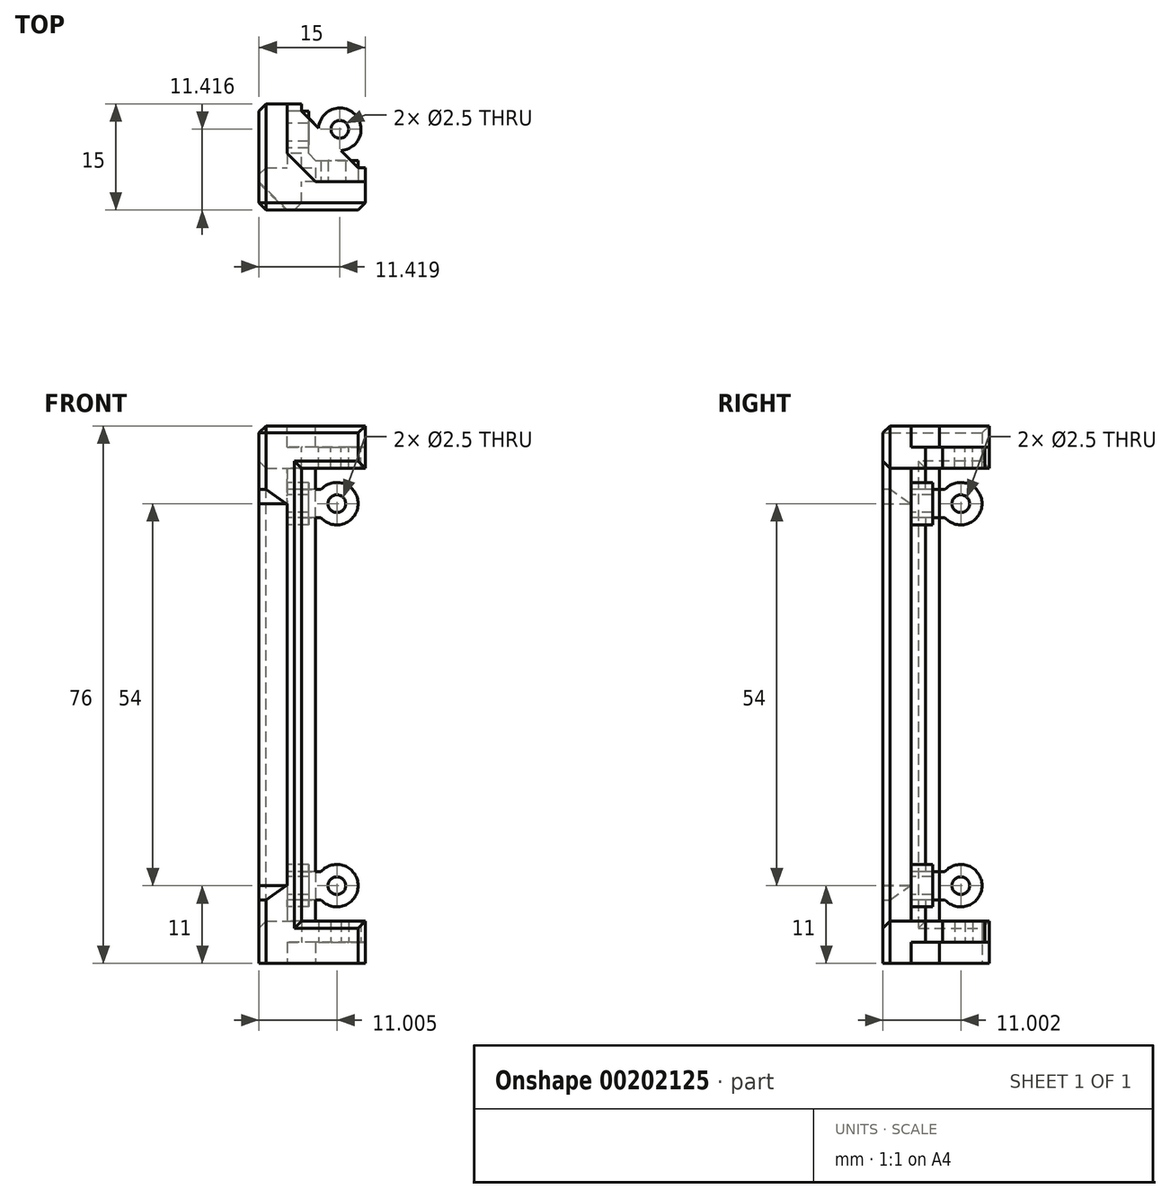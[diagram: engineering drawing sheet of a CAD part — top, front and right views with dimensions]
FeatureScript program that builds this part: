
annotation { "Feature Type Name" : "Feature", "Feature Type Description" : "" }
export const myFeature = defineFeature(function(context is Context, id is Id, definition is map)
    precondition{}
    {
        {
            var Q0;
            Q0=qCreatedBy(makeId("Top.planeOp"),FACE);
            var sketch = newSketch(context, id + "F0", { "sketchPlane" : qUnion([Q0])});
            skLineSegment(sketch, "E0", {"start": v(-30.7, 8.8) * mm, "end": v(-30.7, -6.2) * mm});
            skLineSegment(sketch, "E1", {"start": v(-30.7, -6.2) * mm, "end": v(-15.7, -6.2) * mm});
            skLineSegment(sketch, "E2", {"start": v(-30.7, 8.8) * mm, "end": v(-29.7, 8.8) * mm});
            skLineSegment(sketch, "E3", {"start": v(-15.7, -6.2) * mm, "end": v(-15.7, -5.2) * mm});
            skLineSegment(sketch, "E4", {"start": v(-29.7, 8.8) * mm, "end": v(-24.7, 8.8) * mm});
            skLineSegment(sketch, "E5", {"start": v(-15.7, -5.2) * mm, "end": v(-15.7, -0.2) * mm});
            skLineSegment(sketch, "E6", {"start": v(-24.7, 8.8) * mm, "end": v(-24.7, -0.2) * mm});
            skLineSegment(sketch, "E7", {"start": v(-24.7, -0.2) * mm, "end": v(-15.7, -0.2) * mm});
            skSolve(sketch);
        }
        {
            var Q0;
            Q0=makeQuery(id+"F0.imprint","IMPRINT",FACE,{"disambiguationData":[TD([[makeQuery(id+"F0.imprint","IMPRINT",EDGE,{"derivedFrom":sQuery(id+"F0.wireOp",EDGE,"E0")}),1.0]])]});
            extrude(context, id + "F1", {"entities" : qUnion([Q0]), "depth" : 6 * mm});
        }
        {
            var Q0;
            Q0=makeQuery(id+"F1.opExtrude","CAP_FACE",FACE,{"disambiguationData":[OSD([sQuery(id+"F0.wireOp",EDGE,"E0"),sQuery(id+"F0.wireOp",EDGE,"E1"),sQuery(id+"F0.wireOp",EDGE,"E2"),sQuery(id+"F0.wireOp",EDGE,"E3"),sQuery(id+"F0.wireOp",EDGE,"E4"),sQuery(id+"F0.wireOp",EDGE,"E5"),sQuery(id+"F0.wireOp",EDGE,"E6"),sQuery(id+"F0.wireOp",EDGE,"E7")])],"isStart":false});
            var sketch = newSketch(context, id + "F2", { "sketchPlane" : qUnion([Q0])});
            skLineSegment(sketch, "E8.top", {"start": v(-30.7, -0.2) * mm, "end": v(-24.7, -0.2) * mm});
            skLineSegment(sketch, "E9", {"start": v(-24.7, -0.2) * mm, "end": v(-24.7, 1.8) * mm});
            skLineSegment(sketch, "E10", {"start": v(-24.7, 1.8) * mm, "end": v(-26.7, 1.8) * mm});
            skLineSegment(sketch, "E11", {"start": v(-26.7, 1.8) * mm, "end": v(-26.7, -0.2) * mm});
            skLineSegment(sketch, "E12", {"start": v(-24.7, -0.2) * mm, "end": v(-22.7, -0.2) * mm});
            skLineSegment(sketch, "E13", {"start": v(-22.7, -0.2) * mm, "end": v(-22.7, -2.2) * mm});
            skLineSegment(sketch, "E14", {"start": v(-22.7, -2.2) * mm, "end": v(-24.7, -2.2) * mm});
            skLineSegment(sketch, "E15", {"start": v(-24.7, -6.2) * mm, "end": v(-29.7, -6.2) * mm});
            skLineSegment(sketch, "E16", {"start": v(-24.7, -6.2) * mm, "end": v(-24.7, -2.2) * mm});
            skLineSegment(sketch, "E17", {"start": v(-24.7, -0.2) * mm, "end": v(-24.7, -2.2) * mm});
            skLineSegment(sketch, "E18", {"start": v(-30.7, -0.2) * mm, "end": v(-30.7, -5.2) * mm});
            skLineSegment(sketch, "E19", {"start": v(-30.7, -5.2) * mm, "end": v(-29.7, -6.2) * mm});
            skSolve(sketch);
        }
        {
            var Q0;
            Q0=makeQuery(id+"F2.imprint","IMPRINT",FACE,{"disambiguationData":[TD([[makeQuery(id+"F2.imprint","IMPRINT",EDGE,{"derivedFrom":sQuery(id+"F2.wireOp",EDGE,"E8.bottom")}),1.0]])]});
            var Q1;
            {var subQ0=sQuery(id+"F2.wireOp",EDGE,"E12");Q1=makeQuery(id+"F2.imprint","IMPRINT",FACE,{"disambiguationData":[TD([[makeQuery(id+"F2.imprint","IMPRINT",EDGE,{"derivedFrom":subQ0}),-1.0]])]});}
            var Q2;
            Q2=makeQuery(id+"F2.imprint","IMPRINT",FACE,{"disambiguationData":[TD([[makeQuery(id+"F2.imprint","IMPRINT",EDGE,{"derivedFrom":sQuery(id+"F2.wireOp",EDGE,"E15")}),1.0]])]});
            var Q3;
            {var subQ0=sQuery(id+"F2.wireOp",EDGE,"E9");Q3=makeQuery(id+"F2.imprint","IMPRINT",FACE,{"disambiguationData":[TD([[makeQuery(id+"F2.imprint","IMPRINT",EDGE,{"derivedFrom":subQ0}),-1.0]])]});}
            extrude(context, id + "F3", {"entities" : qUnion([Q0, Q1, Q2, Q3]), "operationType" : NewBodyOperationType.ADD, "depth" : 5 * mm});
        }
        {
            var Q0;
            Q0=makeQuery(id+"F3.opExtrude","CAP_FACE",FACE,{"disambiguationData":[OSD([sQuery(id+"F2.wireOp",EDGE,"E8.bottom"),sQuery(id+"F2.wireOp",EDGE,"E8.top"),sQuery(id+"F2.wireOp",EDGE,"E8.left"),sQuery(id+"F2.wireOp",EDGE,"E8.right"),sQuery(id+"F2.wireOp",EDGE,"E9"),sQuery(id+"F2.wireOp",EDGE,"E10"),sQuery(id+"F2.wireOp",EDGE,"E11"),sQuery(id+"F2.wireOp",EDGE,"E12"),sQuery(id+"F2.wireOp",EDGE,"E13"),sQuery(id+"F2.wireOp",EDGE,"E14")])],"isStart":false});
            var sketch = newSketch(context, id + "F4", { "sketchPlane" : qUnion([Q0])});
            skLineSegment(sketch, "E20", {"start": v(-24.7, -6.2) * mm, "end": v(-26.7, -6.2) * mm});
            skLineSegment(sketch, "E21", {"start": v(-30.7, -0.2) * mm, "end": v(-30.7, -2.2) * mm});
            skLineSegment(sketch, "E22", {"start": v(-26.7, -6.2) * mm, "end": v(-30.7, -2.2) * mm});
            skLineSegment(sketch, "E23", {"start": v(-24.7, -6.2) * mm, "end": v(-24.7, -2.2) * mm});
            skLineSegment(sketch, "E24", {"start": v(-24.7, -2.2) * mm, "end": v(-22.7, -2.2) * mm});
            skLineSegment(sketch, "E25", {"start": v(-22.7, -2.2) * mm, "end": v(-22.7, -0.2) * mm});
            skLineSegment(sketch, "E26", {"start": v(-22.7, -0.2) * mm, "end": v(-24.7, -0.2) * mm});
            skLineSegment(sketch, "E27", {"start": v(-24.7, -0.2) * mm, "end": v(-24.7, 1.8) * mm});
            skLineSegment(sketch, "E28", {"start": v(-24.7, 1.8) * mm, "end": v(-26.7, 1.8) * mm});
            skLineSegment(sketch, "E29", {"start": v(-26.7, 1.8) * mm, "end": v(-26.7, -0.2) * mm});
            skLineSegment(sketch, "E30", {"start": v(-26.7, -0.2) * mm, "end": v(-30.7, -0.2) * mm});
            skSolve(sketch);
        }
        {
            var Q0;
            Q0=makeQuery(id+"F4.imprint","IMPRINT",FACE,{"disambiguationData":[TD([[makeQuery(id+"F4.imprint","IMPRINT",EDGE,{"derivedFrom":sQuery(id+"F4.wireOp",EDGE,"E20")}),1.0]])]});
            extrude(context, id + "F5", {"entities" : qUnion([Q0]), "operationType" : NewBodyOperationType.ADD, "depth" : 27 * mm});
        }
        {
            var Q0;
            Q0=makeQuery(id+"F5.boolean.opBoolean","MERGE",FACE,{"derivedFrom":[makeQuery(id+"F3.opExtrude","SWEPT_FACE",FACE,{"disambiguationData":[OSD([sQuery(id+"F2.wireOp",EDGE,"E14")])]}),makeQuery(id+"F5.opExtrude","SWEPT_FACE",FACE,{"disambiguationData":[OSD([sQuery(id+"FcikvxoAmVT8Sga_1.wireOp",EDGE,"Ugr4Xeua-PaRH-PEAE-46ir-bzMubUFrfAmX")])]})]});
            var sketch = newSketch(context, id + "F6", { "sketchPlane" : qUnion([Q0])});
            skLineSegment(sketch, "E31", {"start": v(-22.7, 6) * mm, "end": v(-22.7, 11) * mm});
            skLineSegment(sketch, "E32", {"start": v(-22.7, 11) * mm, "end": v(-19.7, 11) * mm});
            skCircle(sketch, "E33", {"center": v(-19.7, 11) * mm, "radius": 1.25 * mm});
            skCircle(sketch, "E34", {"center": v(-19.7, 11) * mm, "radius": 3 * mm});
            skLineSegment(sketch, "E35", {"start": v(-22.7, 6) * mm, "end": v(-22.7, 9) * mm});
            skLineSegment(sketch, "E36", {"start": v(-22.7, 9) * mm, "end": v(-21.94, 9) * mm});
            skLineSegment(sketch, "E37", {"start": v(-22.7, 11) * mm, "end": v(-22.7, 13) * mm});
            skLineSegment(sketch, "E38", {"start": v(-22.7, 13) * mm, "end": v(-21.94, 13) * mm});
            skSolve(sketch);
        }
        {
            var Q0;
            Q0=makeQuery(id+"F6.imprint","IMPRINT",FACE,{"disambiguationData":[TD([[makeQuery(id+"F6.imprint","IMPRINT",EDGE,{"derivedFrom":sQuery(id+"F6.wireOp",EDGE,"E33")}),-1.0]])]});
            var Q1;
            {var subQ0=sQuery(id+"F6.wireOp",EDGE,"E37");Q1=makeQuery(id+"F6.imprint","IMPRINT",FACE,{"disambiguationData":[TD([[makeQuery(id+"F6.imprint","IMPRINT",EDGE,{"derivedFrom":subQ0}),1.0]])]});}
            var Q2;
            {var subQ0=sQuery(id+"F6.wireOp",EDGE,"E31");Q2=makeQuery(id+"F6.imprint","IMPRINT",FACE,{"disambiguationData":[TD([[makeQuery(id+"F6.imprint","IMPRINT",EDGE,{"derivedFrom":subQ0}),1.0]])]});}
            extrude(context, id + "F7", {"entities" : qUnion([Q0, Q1, Q2]), "operationType" : NewBodyOperationType.ADD, "oppositeDirection" : true, "depth" : 3 * mm});
        }
        {
            var Q0;
            Q0=makeQuery(id+"F5.boolean.opBoolean","MERGE",FACE,{"derivedFrom":[makeQuery(id+"F3.opExtrude","SWEPT_FACE",FACE,{"disambiguationData":[OSD([sQuery(id+"F2.wireOp",EDGE,"E11")])]}),makeQuery(id+"F5.opExtrude","SWEPT_FACE",FACE,{"disambiguationData":[OSD([sQuery(id+"FcikvxoAmVT8Sga_1.wireOp",EDGE,"rjj8wiBv-6VFg-MGKm-luXr-hqUBBP5AjTz5")])]})]});
            var sketch = newSketch(context, id + "F8", { "sketchPlane" : qUnion([Q0])});
            skLineSegment(sketch, "E39", {"start": v(-1.8, 6) * mm, "end": v(-1.8, 9) * mm});
            skLineSegment(sketch, "E40", {"start": v(-1.8, 9) * mm, "end": v(-1.8, 13) * mm});
            skLineSegment(sketch, "E41", {"start": v(-1.8, 11) * mm, "end": v(-4.8, 11) * mm});
            skCircle(sketch, "E42", {"center": v(-4.8, 11) * mm, "radius": 1.25 * mm});
            skCircle(sketch, "E43", {"center": v(-4.8, 11) * mm, "radius": 3 * mm});
            skLineSegment(sketch, "E44", {"start": v(-1.8, 13) * mm, "end": v(-2.56, 13) * mm});
            skLineSegment(sketch, "E45", {"start": v(-1.8, 9) * mm, "end": v(-2.56, 9) * mm});
            skSolve(sketch);
        }
        {
            var Q0;
            Q0=qSketchRegion(id+"F8",true);
            extrude(context, id + "F9", {"entities" : qUnion([Q0]), "operationType" : NewBodyOperationType.ADD, "oppositeDirection" : true, "depth" : 3 * mm});
        }
        {
            var Q0;
            Q0=makeQuery(id+"F7.opExtrude","SWEPT_FACE",FACE,{"disambiguationData":[OSD([sQuery(id+"F6.wireOp",EDGE,"E38")])]});
            var sketch = newSketch(context, id + "F10", { "sketchPlane" : qUnion([Q0])});
            skLineSegment(sketch, "E46.0", {"start": v(-23.7, 1.8) * mm, "end": v(-24.7, 1.8) * mm});
            skLineSegment(sketch, "E47", {"start": v(-22.7, 0.8) * mm, "end": v(-23.7, 1.8) * mm});
            skLineSegment(sketch, "E48", {"start": v(-24.7, 1.8) * mm, "end": v(-24.7, -0.2) * mm});
            skLineSegment(sketch, "E49", {"start": v(-24.7, -0.2) * mm, "end": v(-22.7, -0.2) * mm});
            skLineSegment(sketch, "E50", {"start": v(-22.7, -0.2) * mm, "end": v(-22.7, 0.8) * mm});
            skSolve(sketch);
        }
        {
            var Q0;
            Q0=makeQuery(id+"F10.imprint","IMPRINT",FACE,{"disambiguationData":[TD([[makeQuery(id+"F10.imprint","IMPRINT",EDGE,{"derivedFrom":sQuery(id+"F10.wireOp",EDGE,"E46.0")}),1.0]])]});
            extrude(context, id + "F11", {"entities" : qUnion([Q0]), "operationType" : NewBodyOperationType.ADD, "oppositeDirection" : true, "depth" : 4 * mm});
        }
        {
            var Q0;
            Q0=makeQuery(id+"F1.opExtrude","CAP_FACE",FACE,{"disambiguationData":[OSD([sQuery(id+"F0.wireOp",EDGE,"E0"),sQuery(id+"F0.wireOp",EDGE,"E1"),sQuery(id+"F0.wireOp",EDGE,"E2"),sQuery(id+"F0.wireOp",EDGE,"E3"),sQuery(id+"F0.wireOp",EDGE,"E4"),sQuery(id+"F0.wireOp",EDGE,"E5"),sQuery(id+"F0.wireOp",EDGE,"E6"),sQuery(id+"F0.wireOp",EDGE,"E7")])],"isStart":true});
            var sketch = newSketch(context, id + "F12", { "sketchPlane" : qUnion([Q0])});
            skLineSegment(sketch, "E51", {"start": v(-15.7, 0.2) * mm, "end": v(-15.7, 2.2) * mm});
            skLineSegment(sketch, "E52", {"start": v(-15.7, 2.2) * mm, "end": v(-22.7, 2.2) * mm});
            skLineSegment(sketch, "E53", {"start": v(-15.7, 0.2) * mm, "end": v(-24.7, 0.2) * mm});
            skLineSegment(sketch, "E54", {"start": v(-24.7, 0.2) * mm, "end": v(-24.7, -8.8) * mm});
            skLineSegment(sketch, "E55", {"start": v(-24.7, -8.8) * mm, "end": v(-26.7, -8.8) * mm});
            skLineSegment(sketch, "E56", {"start": v(-26.7, -8.8) * mm, "end": v(-26.7, -1.8) * mm});
            skLineSegment(sketch, "E57", {"start": v(-22.7, 2.2) * mm, "end": v(-26.7, -1.8) * mm});
            skSolve(sketch);
        }
        {
            var Q0;
            {var subQ0=sQuery(id+"F12.wireOp",EDGE,"E54");Q0=makeQuery(id+"F12.imprint","IMPRINT",FACE,{"disambiguationData":[TD([[makeQuery(id+"F12.imprint","IMPRINT",EDGE,{"derivedFrom":subQ0}),1.0]])]});}
            var Q1;
            Q1=makeQuery(id+"F12.imprint","IMPRINT",FACE,{"disambiguationData":[TD([[makeQuery(id+"F12.imprint","IMPRINT",EDGE,{"derivedFrom":sQuery(id+"F12.wireOp",EDGE,"E51")}),-1.0]])]});
            extrude(context, id + "F13", {"entities" : qUnion([Q0, Q1]), "operationType" : NewBodyOperationType.REMOVE, "oppositeDirection" : true, "depth" : 3 * mm});
        }
        {
            var Q0;
            Q0=makeQuery(id+"F13.boolean.opBoolean","COPY",FACE,{"derivedFrom":makeQuery(id+"F13.opExtrude","CAP_FACE",FACE,{"disambiguationData":[OSD([sQuery(id+"F12.wireOp",EDGE,"E51"),sQuery(id+"F12.wireOp",EDGE,"E52"),sQuery(id+"F12.wireOp",EDGE,"E53"),sQuery(id+"F12.wireOp",EDGE,"E57")])],"isStart":false})});
            var sketch = newSketch(context, id + "F14", { "sketchPlane" : qUnion([Q0])});
            skLineSegment(sketch, "E58", {"start": v(-24.7, 0.2) * mm, "end": v(-24.7, -7.8) * mm});
            skLineSegment(sketch, "E59", {"start": v(-16.7, 0.2) * mm, "end": v(-24.7, -7.8) * mm});
            skLineSegment(sketch, "E60", {"start": v(-20.7, -3.8) * mm, "end": v(-19.3, -5.2) * mm});
            skCircle(sketch, "E61", {"center": v(-19.3, -5.2) * mm, "radius": 1.25 * mm});
            skCircle(sketch, "E62", {"center": v(-19.3, -5.2) * mm, "radius": 3 * mm});
            skLineSegment(sketch, "E63", {"start": v(-16.7, 0.2) * mm, "end": v(-24.7, 0.2) * mm});
            skSolve(sketch);
        }
        {
            var Q0;
            Q0=qSketchRegion(id+"F14",true);
            extrude(context, id + "F15", {"entities" : qUnion([Q0]), "operationType" : NewBodyOperationType.ADD, "oppositeDirection" : true, "depth" : 3 * mm});
        }
        {
            var Q0;
            Q0=makeQuery(id+"F1.opExtrude","SWEPT_BODY",BODY,{"disambiguationData":[OSD([sQuery(id+"F0.wireOp",EDGE,"E0"),sQuery(id+"F0.wireOp",EDGE,"E1"),sQuery(id+"F0.wireOp",EDGE,"E2"),sQuery(id+"F0.wireOp",EDGE,"E3"),sQuery(id+"F0.wireOp",EDGE,"E4"),sQuery(id+"F0.wireOp",EDGE,"E5"),sQuery(id+"F0.wireOp",EDGE,"E6"),sQuery(id+"F0.wireOp",EDGE,"E7")])]});
            var Q1;
            Q1=makeQuery(id+"F5.opExtrude","CAP_FACE",FACE,{"disambiguationData":[OSD([sQuery(id+"F4.wireOp",EDGE,"E20"),sQuery(id+"F4.wireOp",EDGE,"E21"),sQuery(id+"F4.wireOp",EDGE,"E22"),sQuery(id+"F4.wireOp",EDGE,"E23"),sQuery(id+"F4.wireOp",EDGE,"E24"),sQuery(id+"F4.wireOp",EDGE,"E25"),sQuery(id+"F4.wireOp",EDGE,"E26"),sQuery(id+"F4.wireOp",EDGE,"E27"),sQuery(id+"F4.wireOp",EDGE,"E28"),sQuery(id+"F4.wireOp",EDGE,"E29"),sQuery(id+"F4.wireOp",EDGE,"E30")])],"isStart":false});
            mirror(context, id + "F16", {"operationType" : NewBodyOperationType.ADD, "entities" : qUnion([Q0]), "mirrorPlane" : qUnion([Q1])});
        }
        {
            var Q0;
            Q0=makeQuery(id+"FhzFfjnD5mDQNPN_1.boolean.opBoolean","MERGE",EDGE,{"derivedFrom":[makeQuery(id+"FrQZREyW5eWcuGQ_1.boolean.opBoolean","MERGE",EDGE,{"derivedFrom":[makeQuery(id+"F1.opExtrude","SWEPT_EDGE",EDGE,{"disambiguationData":[OSD([sQuery(id+"F0.wireOp",EDGE,"E0"),sQuery(id+"F0.wireOp",EDGE,"E1")])]}),makeQuery(id+"FrQZREyW5eWcuGQ_1.opExtrude","SWEPT_EDGE",EDGE,{"disambiguationData":[OSD([sQuery(id+"FOzdUzQN7WSNxo8_1.wireOp",EDGE,"WiYNZVCE-U4Jg-TT48-NUzQ-lxR1TrsUEIwd"),sQuery(id+"FOzdUzQN7WSNxo8_1.wireOp",EDGE,"8d8B1xfc-AYmp-EXSV-HG8z-yugG2Eprzqf7")])]})]}),makeQuery(id+"FhzFfjnD5mDQNPN_1.opExtrude","CAP_EDGE",EDGE,{"disambiguationData":[OSD([sQuery(id+"FUuBHju1a3qaWlO_1.wireOp",EDGE,"Y2hAY4q1-hRi0-7PEO-YUI0-E3ofIxBZuGLo")])],"isStart":true})]});
            var Q1;
            {var subQ0=makeQuery(id+"F5.boolean.opBoolean","MERGE",EDGE,{"derivedFrom":[makeQuery(id+"F3.opExtrude","SWEPT_EDGE",EDGE,{"disambiguationData":[OSD([sQuery(id+"F0.wireOp",EDGE,"E1"),sQuery(id+"F2.wireOp",EDGE,"E15"),sQuery(id+"F2.wireOp",EDGE,"E16")])]}),makeQuery(id+"F5.opExtrude","SWEPT_EDGE",EDGE,{"disambiguationData":[OSD([sQuery(id+"F4.wireOp",EDGE,"E20"),sQuery(id+"F4.wireOp",EDGE,"E23")])]})]});Q1=makeQuery(id+"F16.boolean.opBoolean","MERGE",EDGE,{"derivedFrom":[subQ0,makeQuery(id+"F16.opPattern","COPY",EDGE,{"derivedFrom":subQ0,"instanceName":"1"})]});}
            var Q2;
            {var subQ0=sQuery(id+"F0.wireOp",EDGE,"E1");Q2=makeQuery(id+"F3.boolean.opBoolean","SPLIT",EDGE,{"disambiguationData":[TD([makeQuery(id+"F3.opExtrude","SWEPT_FACE",FACE,{"disambiguationData":[OSD([sQuery(id+"F2.wireOp",EDGE,"E16")])]})])],"derivedFrom":makeQuery(id+"F1.opExtrude","CAP_EDGE",EDGE,{"disambiguationData":[OSD([subQ0])],"isStart":false})});}
            var Q3;
            {var subQ2=sQuery(id+"F0.wireOp",EDGE,"E0");Q3=makeQuery(id+"F3.boolean.opBoolean","SPLIT",EDGE,{"disambiguationData":[TD([makeQuery(id+"F3.opExtrude","SWEPT_FACE",FACE,{"disambiguationData":[OSD([sQuery(id+"F2.wireOp",EDGE,"E8.top")])]})])],"derivedFrom":makeQuery(id+"F1.opExtrude","CAP_EDGE",EDGE,{"disambiguationData":[OSD([subQ2])],"isStart":false})});}
            var Q4;
            {var subQ0=makeQuery(id+"F5.boolean.opBoolean","MERGE",EDGE,{"derivedFrom":[makeQuery(id+"F3.opExtrude","SWEPT_EDGE",EDGE,{"disambiguationData":[OSD([sQuery(id+"F0.wireOp",EDGE,"E0"),sQuery(id+"F2.wireOp",EDGE,"E8.top"),sQuery(id+"F2.wireOp",EDGE,"E18")])]}),makeQuery(id+"F5.opExtrude","SWEPT_EDGE",EDGE,{"disambiguationData":[OSD([sQuery(id+"F4.wireOp",EDGE,"E21"),sQuery(id+"F4.wireOp",EDGE,"E30")])]})]});Q4=makeQuery(id+"F16.boolean.opBoolean","MERGE",EDGE,{"derivedFrom":[subQ0,makeQuery(id+"F16.opPattern","COPY",EDGE,{"derivedFrom":subQ0,"instanceName":"1"})]});}
            var Q5;
            {var subQ2=sQuery(id+"F0.wireOp",EDGE,"E0");Q5=makeQuery(id+"F16.opPattern","COPY",EDGE,{"derivedFrom":makeQuery(id+"F3.boolean.opBoolean","SPLIT",EDGE,{"disambiguationData":[TD([makeQuery(id+"F3.opExtrude","SWEPT_FACE",FACE,{"disambiguationData":[OSD([sQuery(id+"F2.wireOp",EDGE,"E8.top")])]})])],"derivedFrom":makeQuery(id+"F1.opExtrude","CAP_EDGE",EDGE,{"disambiguationData":[OSD([subQ2])],"isStart":false})}),"instanceName":"1"});}
            var Q6;
            {var subQ0=sQuery(id+"F0.wireOp",EDGE,"E1");Q6=makeQuery(id+"F16.opPattern","COPY",EDGE,{"derivedFrom":makeQuery(id+"F3.boolean.opBoolean","SPLIT",EDGE,{"disambiguationData":[TD([makeQuery(id+"F3.opExtrude","SWEPT_FACE",FACE,{"disambiguationData":[OSD([sQuery(id+"F2.wireOp",EDGE,"E16")])]})])],"derivedFrom":makeQuery(id+"F1.opExtrude","CAP_EDGE",EDGE,{"disambiguationData":[OSD([subQ0])],"isStart":false})}),"instanceName":"1"});}
            var Q7;
            Q7=makeQuery(id+"F16.opPattern","COPY",EDGE,{"derivedFrom":makeQuery(id+"F1.opExtrude","SWEPT_EDGE",EDGE,{"disambiguationData":[OSD([sQuery(id+"F0.wireOp",EDGE,"E1"),sQuery(id+"F0.wireOp",EDGE,"E3")])]}),"instanceName":"1"});
            var Q8;
            Q8=makeQuery(id+"F16.opPattern","COPY",EDGE,{"derivedFrom":makeQuery(id+"F1.opExtrude","SWEPT_EDGE",EDGE,{"disambiguationData":[OSD([sQuery(id+"F0.wireOp",EDGE,"E0"),sQuery(id+"F0.wireOp",EDGE,"E2")])]}),"instanceName":"1"});
            var Q9;
            Q9=makeQuery(id+"FrQZREyW5eWcuGQ_1.boolean.opBoolean","MERGE",EDGE,{"derivedFrom":[makeQuery(id+"F1.opExtrude","SWEPT_EDGE",EDGE,{"disambiguationData":[OSD([sQuery(id+"F0.wireOp",EDGE,"E0"),sQuery(id+"F0.wireOp",EDGE,"E2")])]}),makeQuery(id+"FrQZREyW5eWcuGQ_1.opExtrude","SWEPT_EDGE",EDGE,{"disambiguationData":[OSD([sQuery(id+"FOzdUzQN7WSNxo8_1.wireOp",EDGE,"bvd9bl0E-zov9-mno0-jdsr-QOLO0tRtuMB9"),sQuery(id+"FOzdUzQN7WSNxo8_1.wireOp",EDGE,"WiYNZVCE-U4Jg-TT48-NUzQ-lxR1TrsUEIwd")])]})]});
            var Q10;
            Q10=makeQuery(id+"FrQZREyW5eWcuGQ_1.boolean.opBoolean","MERGE",EDGE,{"derivedFrom":[makeQuery(id+"F1.opExtrude","SWEPT_EDGE",EDGE,{"disambiguationData":[OSD([sQuery(id+"F0.wireOp",EDGE,"E1"),sQuery(id+"F0.wireOp",EDGE,"E3")])]}),makeQuery(id+"FrQZREyW5eWcuGQ_1.opExtrude","SWEPT_EDGE",EDGE,{"disambiguationData":[OSD([sQuery(id+"FOzdUzQN7WSNxo8_1.wireOp",EDGE,"8d8B1xfc-AYmp-EXSV-HG8z-yugG2Eprzqf7"),sQuery(id+"FOzdUzQN7WSNxo8_1.wireOp",EDGE,"MSLuVhra-DmRv-DVba-FcVb-sEYbxNxOgFvK")])]})]});
            var Q11;
            Q11=makeQuery(id+"FhzFfjnD5mDQNPN_1.opExtrude","CAP_EDGE",EDGE,{"disambiguationData":[OSD([sQuery(id+"FUuBHju1a3qaWlO_1.wireOp",EDGE,"4F8UiIUv-5H1C-12AU-MrLI-4g8t5kWoGJfL")])],"isStart":true});
            var Q12;
            Q12=makeQuery(id+"FLNWeMOsxUtLRx3_1.boolean.opBoolean","MERGE",EDGE,{"derivedFrom":[makeQuery(id+"FhzFfjnD5mDQNPN_1.opExtrude","SWEPT_EDGE",EDGE,{"disambiguationData":[OSD([sQuery(id+"FUuBHju1a3qaWlO_1.wireOp",EDGE,"Y2hAY4q1-hRi0-7PEO-YUI0-E3ofIxBZuGLo"),sQuery(id+"FUuBHju1a3qaWlO_1.wireOp",EDGE,"4F8UiIUv-5H1C-12AU-MrLI-4g8t5kWoGJfL")])]}),makeQuery(id+"FLNWeMOsxUtLRx3_1.opExtrude","CAP_EDGE",EDGE,{"disambiguationData":[OSD([sQuery(id+"FLM7EheutEo60uB_1.wireOp",EDGE,"BrBLu7pY-tHSo-Owc5-F9vD-osR30emi00rM")])],"isStart":true})]});
            var Q13;
            Q13=makeQuery(id+"F16.opPattern","COPY",EDGE,{"derivedFrom":makeQuery(id+"F1.opExtrude","CAP_EDGE",EDGE,{"disambiguationData":[OSD([sQuery(id+"F0.wireOp",EDGE,"E1")])],"isStart":true}),"instanceName":"1"});
            var Q14;
            Q14=makeQuery(id+"F16.opPattern","COPY",EDGE,{"derivedFrom":makeQuery(id+"F1.opExtrude","SWEPT_EDGE",EDGE,{"disambiguationData":[OSD([sQuery(id+"F0.wireOp",EDGE,"E0"),sQuery(id+"F0.wireOp",EDGE,"E1")])]}),"instanceName":"1"});
            var Q15;
            Q15=makeQuery(id+"F16.opPattern","COPY",EDGE,{"derivedFrom":makeQuery(id+"F1.opExtrude","CAP_EDGE",EDGE,{"disambiguationData":[OSD([sQuery(id+"F0.wireOp",EDGE,"E0")])],"isStart":true}),"instanceName":"1"});
            chamfer(context, id + "F17", {"entities" : qUnion([Q0, Q1, Q2, Q3, Q4, Q5, Q6, Q7, Q8, Q9, Q10, Q11, Q12, Q13, Q14, Q15]), "width" : 1 * mm, "tangentPropagation" : true});
        }
        {
            var Q0;
            Q0=makeQuery(id+"F3.opExtrude","CAP_EDGE",EDGE,{"disambiguationData":[OSD([sQuery(id+"F2.wireOp",EDGE,"E19")])],"isStart":false});
            var Q1;
            Q1=makeQuery(id+"F16.opPattern","COPY",EDGE,{"derivedFrom":makeQuery(id+"F3.opExtrude","CAP_EDGE",EDGE,{"disambiguationData":[OSD([sQuery(id+"F2.wireOp",EDGE,"E19")])],"isStart":false}),"instanceName":"1"});
            chamfer(context, id + "F18", {"entities" : qUnion([Q0, Q1]), "width" : 2 * mm, "tangentPropagation" : true});
        }
    });
